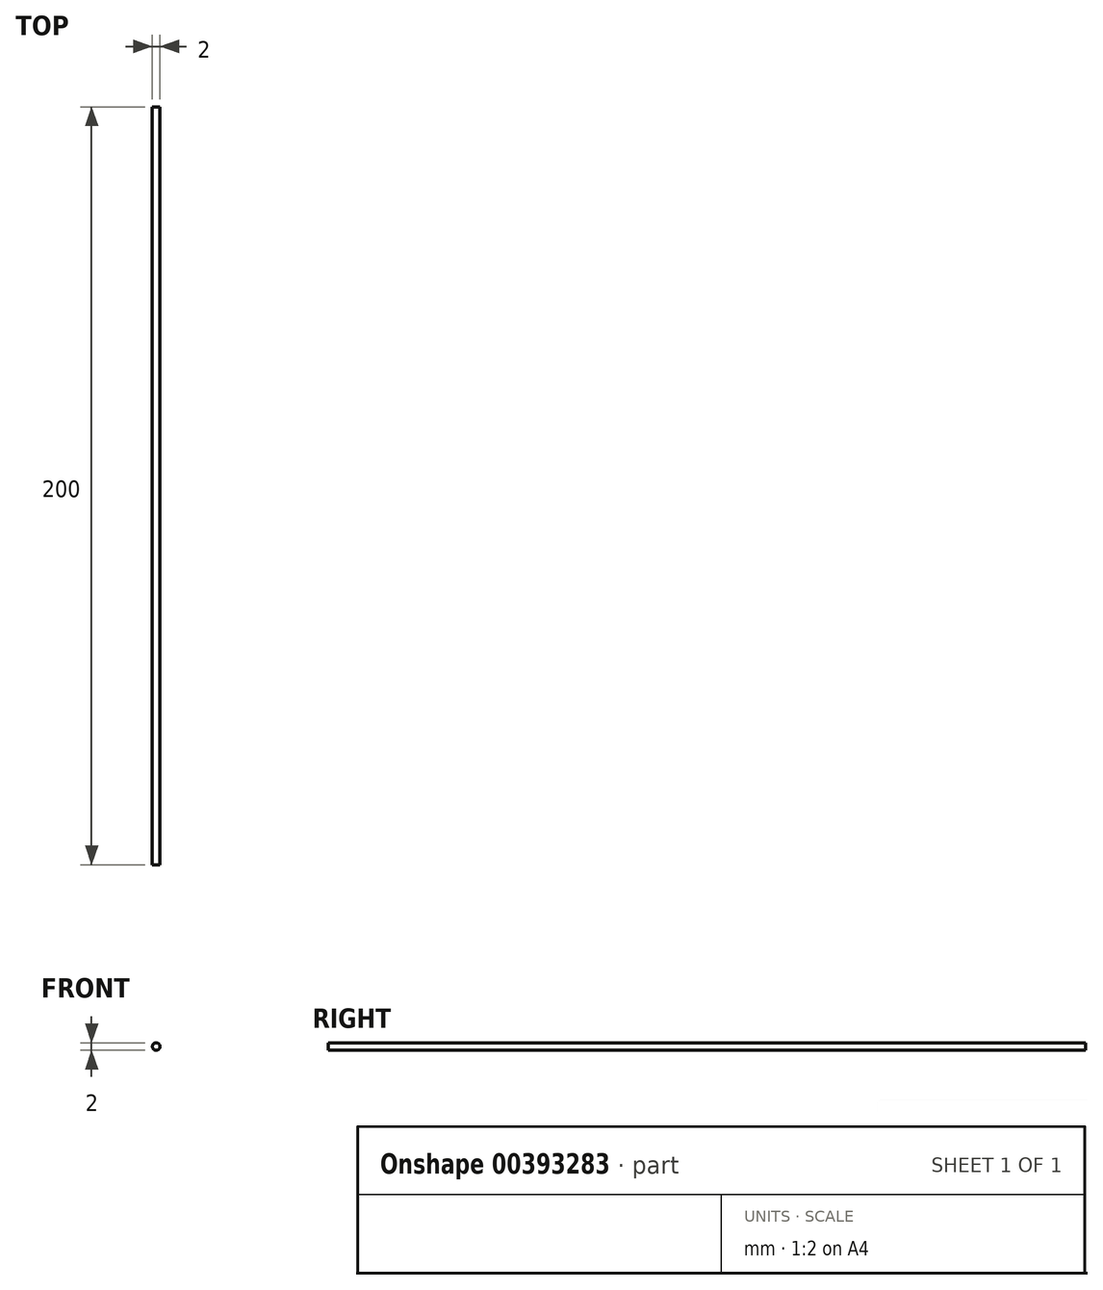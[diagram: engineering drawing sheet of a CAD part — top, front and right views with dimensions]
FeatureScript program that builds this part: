
annotation { "Feature Type Name" : "Feature", "Feature Type Description" : "" }
export const myFeature = defineFeature(function(context is Context, id is Id, definition is map)
    precondition{}
    {
        {
            var Q0;
            Q0=qCreatedBy(makeId("Front.planeOp"),FACE);
            var sketch = newSketch(context, id + "F0", { "sketchPlane" : qUnion([Q0])});
            skCircle(sketch, "E0", {"center": v(0, 0) * mm, "radius": 1 * mm});
            skSolve(sketch);
        }
        {
            var Q0;
            Q0=makeQuery(id+"F0.imprint","IMPRINT",FACE,{"disambiguationData":[TD([[makeQuery(id+"F0.imprint","IMPRINT",EDGE,{"derivedFrom":sQuery(id+"F0.wireOp",EDGE,"E0")}),1.0]])]});
            extrude(context, id + "F1", {"entities" : qUnion([Q0]), "depth" : 200 * mm});
        }
    });
